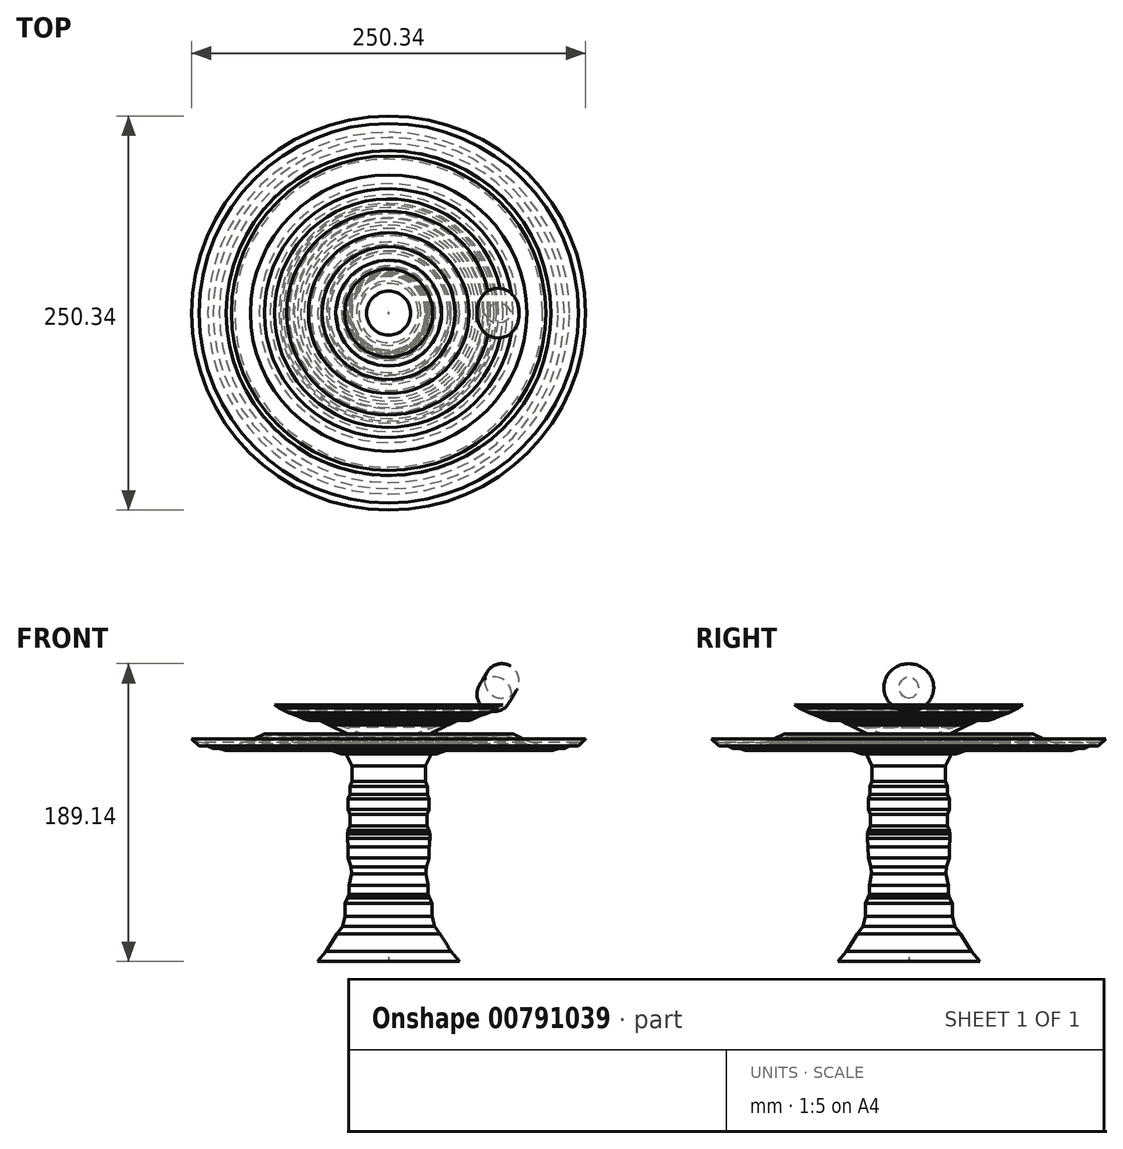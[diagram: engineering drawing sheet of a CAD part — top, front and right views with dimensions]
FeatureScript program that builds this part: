
annotation { "Feature Type Name" : "Feature", "Feature Type Description" : "" }
export const myFeature = defineFeature(function(context is Context, id is Id, definition is map)
    precondition{}
    {
        {
            var Q0;
            Q0=qCreatedBy(makeId("Front.planeOp"),FACE);
            var sketch = newSketch(context, id + "F0", { "sketchPlane" : qUnion([Q0])});
            skLineSegment(sketch, "E0", {"start": v(-23.36, 74.97) * mm, "end": v(-23.36, -65.8) * mm});
            skLineSegment(sketch, "E1", {"start": v(-23.36, 74.97) * mm, "end": v(-19, 74.97) * mm});
            skLineSegment(sketch, "E2", {"start": v(-19, 74.97) * mm, "end": v(-9.36, 74.97) * mm});
            skLineSegment(sketch, "E3", {"start": v(-9.36, 74.97) * mm, "end": v(4.63, 79.97) * mm});
            skLineSegment(sketch, "E4", {"start": v(4.63, 79.97) * mm, "end": v(10.25, 81.62) * mm});
            skLineSegment(sketch, "E5", {"start": v(10.25, 81.62) * mm, "end": v(18.84, 85.98) * mm});
            skLineSegment(sketch, "E6", {"start": v(18.84, 85.98) * mm, "end": v(27.65, 85.98) * mm});
            skLineSegment(sketch, "E7", {"start": v(27.65, 85.98) * mm, "end": v(41.36, 90.39) * mm});
            skLineSegment(sketch, "E8", {"start": v(41.36, 90.39) * mm, "end": v(49.2, 94.3) * mm});
            skLineSegment(sketch, "E9", {"start": v(49.2, 94.3) * mm, "end": v(46.35, 92.35) * mm});
            skPoint(sketch, "E9.endSnap0", {"position": v(45.28, 92.35) * mm});
            skLineSegment(sketch, "E10", {"start": v(46.35, 92.35) * mm, "end": v(42.43, 90.39) * mm});
            skLineSegment(sketch, "E11", {"start": v(42.43, 90.39) * mm, "end": v(39.8, 89.07) * mm});
            skLineSegment(sketch, "E12", {"start": v(39.8, 89.07) * mm, "end": v(34.5, 87.37) * mm});
            skPoint(sketch, "E12.endSnap0", {"position": v(34.5, 88.18) * mm});
            skLineSegment(sketch, "E13", {"start": v(34.5, 87.37) * mm, "end": v(30.4, 85.31) * mm});
            skLineSegment(sketch, "E14", {"start": v(30.4, 85.31) * mm, "end": v(27.03, 84.23) * mm});
            skLineSegment(sketch, "E15", {"start": v(27.03, 84.23) * mm, "end": v(20.1, 84.23) * mm});
            skLineSegment(sketch, "E16", {"start": v(20.1, 84.23) * mm, "end": v(17.34, 82.85) * mm});
            skLineSegment(sketch, "E17", {"start": v(17.34, 82.85) * mm, "end": v(15.77, 82.07) * mm});
            skLineSegment(sketch, "E18", {"start": v(15.77, 82.07) * mm, "end": v(14.37, 81.62) * mm});
            skLineSegment(sketch, "E19", {"start": v(14.37, 81.62) * mm, "end": v(-4.52, 72.17) * mm});
            skLineSegment(sketch, "E20", {"start": v(-4.52, 72.17) * mm, "end": v(-2.85, 68.82) * mm});
            skLineSegment(sketch, "E21", {"start": v(-2.85, 68.82) * mm, "end": v(10.25, 68.82) * mm});
            skLineSegment(sketch, "E22", {"start": v(10.25, 68.82) * mm, "end": v(25.88, 73.85) * mm});
            skLineSegment(sketch, "E23", {"start": v(25.88, 73.85) * mm, "end": v(37.29, 73.85) * mm});
            skLineSegment(sketch, "E24", {"start": v(37.29, 73.85) * mm, "end": v(43.6, 75.88) * mm});
            skLineSegment(sketch, "E25", {"start": v(43.6, 75.88) * mm, "end": v(55.6, 75.88) * mm});
            skLineSegment(sketch, "E26", {"start": v(55.6, 75.88) * mm, "end": v(64.42, 71.57) * mm});
            skLineSegment(sketch, "E27", {"start": v(64.42, 71.57) * mm, "end": v(76.5, 67.97) * mm});
            skLineSegment(sketch, "E28", {"start": v(76.5, 67.97) * mm, "end": v(79.78, 67.65) * mm});
            skLineSegment(sketch, "E29", {"start": v(79.78, 67.65) * mm, "end": v(97.1, 70.26) * mm});
            skLineSegment(sketch, "E30", {"start": v(97.1, 70.26) * mm, "end": v(106.52, 74.97) * mm});
            skLineSegment(sketch, "E31", {"start": v(106.52, 74.97) * mm, "end": v(101.8, 72.62) * mm});
            skLineSegment(sketch, "E32", {"start": v(101.8, 72.62) * mm, "end": v(97.1, 68.14) * mm});
            skLineSegment(sketch, "E33", {"start": v(97.1, 68.14) * mm, "end": v(91.5, 68.14) * mm});
            skLineSegment(sketch, "E34", {"start": v(91.5, 68.14) * mm, "end": v(88.17, 66.47) * mm});
            skLineSegment(sketch, "E35", {"start": v(88.17, 66.47) * mm, "end": v(84.22, 66.47) * mm});
            skLineSegment(sketch, "E36", {"start": v(84.22, 66.47) * mm, "end": v(80.27, 65.2) * mm});
            skLineSegment(sketch, "E37", {"start": v(80.27, 65.2) * mm, "end": v(74.5, 66.77) * mm});
            skLineSegment(sketch, "E38", {"start": v(74.5, 66.77) * mm, "end": v(64.32, 69.35) * mm});
            skLineSegment(sketch, "E39", {"start": v(64.32, 69.35) * mm, "end": v(58.85, 72.54) * mm});
            skLineSegment(sketch, "E40", {"start": v(58.85, 72.54) * mm, "end": v(55.52, 73.45) * mm});
            skLineSegment(sketch, "E41", {"start": v(55.52, 73.45) * mm, "end": v(51.89, 74.44) * mm});
            skLineSegment(sketch, "E42", {"start": v(51.89, 74.44) * mm, "end": v(45.18, 74.44) * mm});
            skLineSegment(sketch, "E43", {"start": v(45.18, 74.44) * mm, "end": v(40.18, 72.65) * mm});
            skLineSegment(sketch, "E44", {"start": v(40.18, 72.65) * mm, "end": v(36.68, 70.11) * mm});
            skLineSegment(sketch, "E45", {"start": v(36.68, 70.11) * mm, "end": v(32.5, 71.25) * mm});
            skLineSegment(sketch, "E46", {"start": v(32.5, 71.25) * mm, "end": v(25.92, 68.9) * mm});
            skLineSegment(sketch, "E47", {"start": v(25.92, 68.9) * mm, "end": v(16.32, 66.47) * mm});
            skLineSegment(sketch, "E48", {"start": v(16.32, 66.47) * mm, "end": v(6.52, 62.96) * mm});
            skLineSegment(sketch, "E49", {"start": v(6.52, 62.96) * mm, "end": v(3.96, 63.66) * mm});
            skLineSegment(sketch, "E50", {"start": v(3.96, 63.66) * mm, "end": v(0, 55.55) * mm});
            skLineSegment(sketch, "E51", {"start": v(0, 55.55) * mm, "end": v(0, 45.7) * mm});
            skLineSegment(sketch, "E52", {"start": v(0, 45.7) * mm, "end": v(1.26, 42.44) * mm});
            skLineSegment(sketch, "E53", {"start": v(1.26, 42.44) * mm, "end": v(1.26, 37.5) * mm});
            skLineSegment(sketch, "E54", {"start": v(1.26, 37.5) * mm, "end": v(2.34, 34.53) * mm});
            skLineSegment(sketch, "E55", {"start": v(2.34, 34.53) * mm, "end": v(2.34, 29.38) * mm});
            skLineSegment(sketch, "E56", {"start": v(2.34, 29.38) * mm, "end": v(2.34, 27.74) * mm});
            skLineSegment(sketch, "E57", {"start": v(2.34, 27.74) * mm, "end": v(1.1, 24.81) * mm});
            skLineSegment(sketch, "E58", {"start": v(1.1, 24.81) * mm, "end": v(1.1, 22.47) * mm});
            skLineSegment(sketch, "E59", {"start": v(1.1, 22.47) * mm, "end": v(1.1, 17.5) * mm});
            skLineSegment(sketch, "E60", {"start": v(1.1, 17.5) * mm, "end": v(2.34, 14.42) * mm});
            skLineSegment(sketch, "E61", {"start": v(2.34, 14.42) * mm, "end": v(2.85, 12.22) * mm});
            skLineSegment(sketch, "E62", {"start": v(2.85, 12.22) * mm, "end": v(2.85, 9.44) * mm});
            skLineSegment(sketch, "E63", {"start": v(2.85, 9.44) * mm, "end": v(2.41, 4.02) * mm});
            skLineSegment(sketch, "E64", {"start": v(2.41, 4.02) * mm, "end": v(2.34, -3.04) * mm});
            skLineSegment(sketch, "E65", {"start": v(2.34, -3.04) * mm, "end": v(0.6, -8.7) * mm});
            skLineSegment(sketch, "E66", {"start": v(0.6, -8.7) * mm, "end": v(0.31, -12.95) * mm});
            skLineSegment(sketch, "E67", {"start": v(0.31, -12.95) * mm, "end": v(1.73, -20.3) * mm});
            skLineSegment(sketch, "E68", {"start": v(1.73, -20.3) * mm, "end": v(1.73, -26.24) * mm});
            skLineSegment(sketch, "E69", {"start": v(1.73, -26.24) * mm, "end": v(2.58, -28.22) * mm});
            skLineSegment(sketch, "E70", {"start": v(2.58, -28.22) * mm, "end": v(4.28, -31.9) * mm});
            skLineSegment(sketch, "E71", {"start": v(4.28, -31.9) * mm, "end": v(4.28, -40.16) * mm});
            skLineSegment(sketch, "E72", {"start": v(4.28, -40.16) * mm, "end": v(5.84, -46.5) * mm});
            skLineSegment(sketch, "E73", {"start": v(5.84, -46.5) * mm, "end": v(9.33, -51.27) * mm});
            skLineSegment(sketch, "E74", {"start": v(9.33, -51.27) * mm, "end": v(16.31, -62.37) * mm});
            skLineSegment(sketch, "E75", {"start": v(16.31, -62.37) * mm, "end": v(21.7, -68.71) * mm});
            skLineSegment(sketch, "E76", {"start": v(21.7, -68.71) * mm, "end": v(-23.03, -68.71) * mm});
            skLineSegment(sketch, "E77", {"start": v(-23.03, -68.71) * mm, "end": v(-23.36, -65.8) * mm});
            skSolve(sketch);
        }
        {
            var Q0;
            Q0 = qSketchRegion(id + "F0", true);
            var Q1;
            Q1=sQuery(id+"F0.wireOp",EDGE,"E0");
            revolve(context, id + "F1", {"surfaceOperationType" : NewSurfaceOperationType.NEW, "entities" : qUnion([Q0]), "axis" : qUnion([Q1]), "revolveType" : RevolveType.FULL});
        }
        {
            var Q0;
            Q0=qCreatedBy(makeId("Front.planeOp"),FACE);
            var sketch = newSketch(context, id + "F2", { "sketchPlane" : qUnion([Q0])});
            skLineSegment(sketch, "E78", {"start": v(37.62, 110.25) * mm, "end": v(54.6, 100.3) * mm});
            skArc(sketch, "E79", {"start": v(54.6, 100.3) * mm, "mid": v(49.2, 110.55) * mm, "end": v(37.62, 110.25) * mm});
            skSolve(sketch);
        }
        {
            var Q0;
            Q0 = qSketchRegion(id + "F2", true);
            var Q1;
            Q1=sQuery(id+"F2.wireOp",EDGE,"E78");
            revolve(context, id + "F3", {"surfaceOperationType" : NewSurfaceOperationType.NEW, "entities" : qUnion([Q0]), "axis" : qUnion([Q1]), "revolveType" : RevolveType.FULL});
        }
    });
